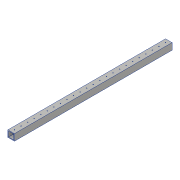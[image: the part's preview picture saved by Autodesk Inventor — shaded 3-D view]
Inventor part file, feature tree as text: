
AUTODESK INVENTOR PART (.ipt)
format: ipt  version: 2018 (Build 220112000, 112)  size: 138,240 bytes
history: native  units: in
note: dims shown in document units (in); Inventor stores cm internally (conversion verified against a paired STEP export)
features: sketch x2, extrude x1, shell x1, hole x1
ambient origin geometry x8: Origin, YZ Plane, XZ Plane, XY Plane, X Axis, Y Axis, Z Axis, Center Point
bodies: Solid1 (feature_tree)
feature tree (5):
  extrude  "Extrusion1"  Depth=1.0in
  shell  "Shell1"  Thickness=24.0in
  hole  "Hole1"  [1 undecoded]
  sketch  "Sketch1"  dims[d0=1.0in d1=1.0in d2=24.0in d3=0.0in]
  sketch  "Sketch2"  dims[d4=0.1in d5=0.5in d6=0.5in d7=14.5669in d9=1.0in d10=0.3937in d12=1.0in d14=0.1in d15=0.75in d16=0.375in d17=0.25in d18=0.5635in d19=2.0in d20=0.8108in]
note: 1 required parameter value undecoded (feature->parameter linkage not recoverable at this tier; creation-order binding heuristic only, values carry confidence <= 0.55)
